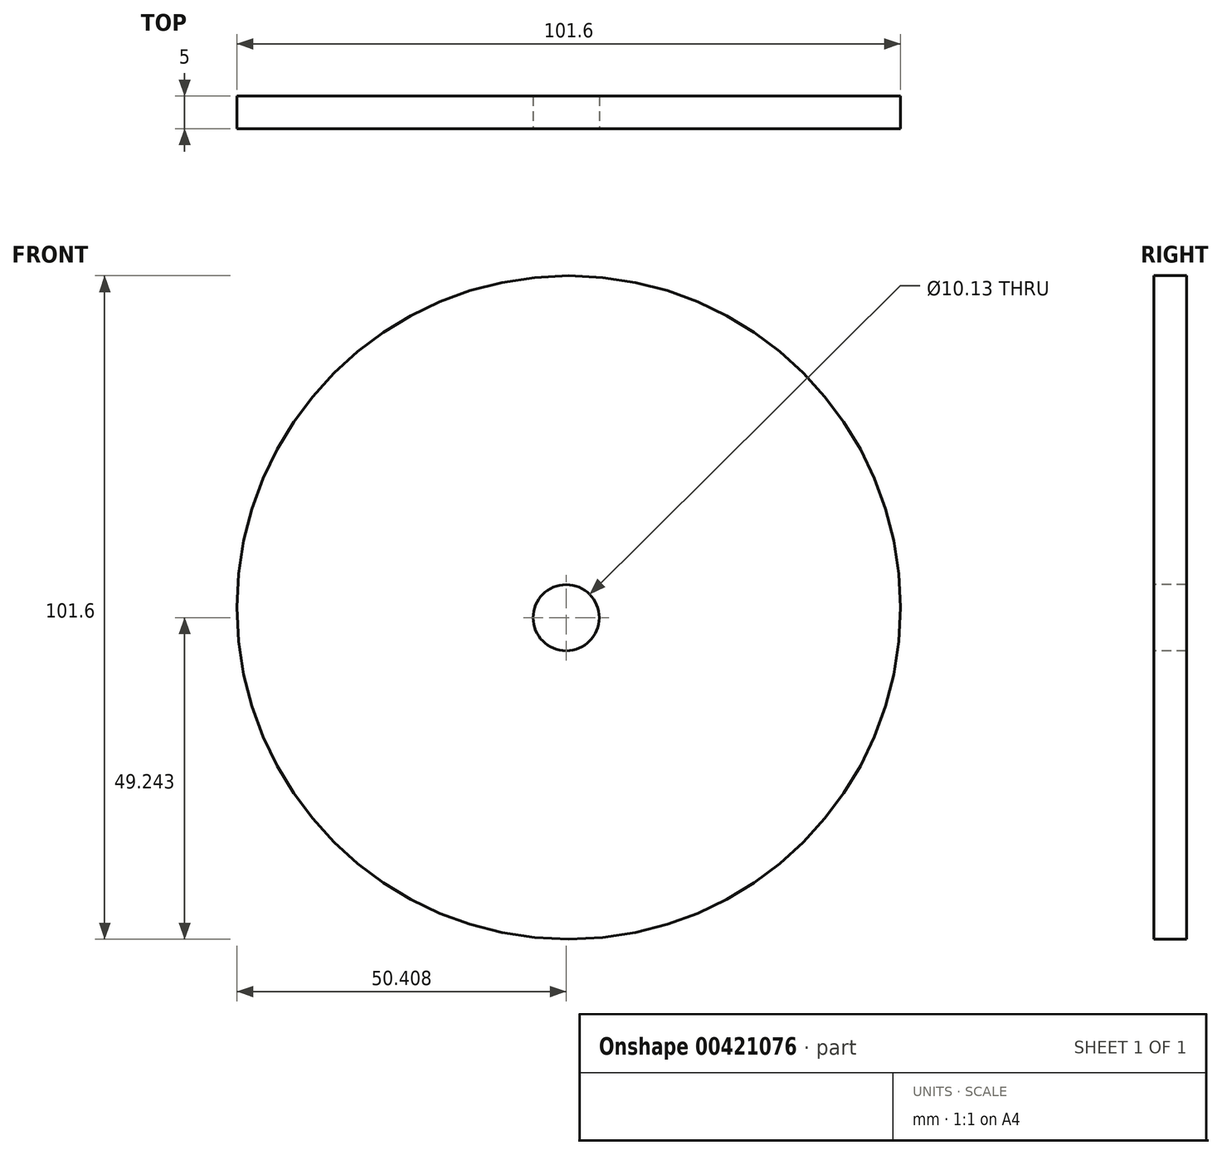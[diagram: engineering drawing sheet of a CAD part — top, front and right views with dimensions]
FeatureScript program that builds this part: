
annotation { "Feature Type Name" : "Feature", "Feature Type Description" : "" }
export const myFeature = defineFeature(function(context is Context, id is Id, definition is map)
    precondition{}
    {
        {
            var Q0;
            Q0=qCreatedBy(makeId("Front.planeOp"),FACE);
            var sketch = newSketch(context, id + "F0", { "sketchPlane" : qUnion([Q0])});
            skCircle(sketch, "E0", {"center": v(-20.32, 98.2) * mm, "radius": 50.8 * mm});
            skSolve(sketch);
        }
        {
            var Q0;
            Q0=makeQuery(id+"F0.imprint","IMPRINT",FACE,{"disambiguationData":[TD([[makeQuery(id+"F0.imprint","IMPRINT",EDGE,{"derivedFrom":sQuery(id+"F0.wireOp",EDGE,"E0")}),1.0]])]});
            extrude(context, id + "F1", {"entities" : qUnion([Q0]), "depth" : 5 * mm});
        }
        {
            var Q0;
            Q0=makeQuery(id+"F1.opExtrude","CAP_FACE",FACE,{"disambiguationData":[OSD([sQuery(id+"F0.wireOp",EDGE,"E0")])],"isStart":false});
            var sketch = newSketch(context, id + "F2", { "sketchPlane" : qUnion([Q0])});
            skCircle(sketch, "E1", {"center": v(-20.32, 98.2) * mm, "radius": 11.29 * mm});
            skSolve(sketch);
        }
        {
            var Q0;
            Q0=makeQuery(id+"F2.imprint","IMPRINT",FACE,{"disambiguationData":[TD([[makeQuery(id+"F2.imprint","IMPRINT",EDGE,{"derivedFrom":sQuery(id+"F2.wireOp",EDGE,"E1")}),1.0]])]});
            var sketch = newSketch(context, id + "F3", { "sketchPlane" : qUnion([Q0])});
            skCircle(sketch, "E2", {"center": v(-20.71, 96.65) * mm, "radius": 5.06 * mm});
            skSolve(sketch);
        }
        {
            var Q0;
            Q0=makeQuery(id+"F3.imprint","IMPRINT",FACE,{"disambiguationData":[TD([[makeQuery(id+"F3.imprint","IMPRINT",EDGE,{"derivedFrom":sQuery(id+"F3.wireOp",EDGE,"E2")}),1.0]])]});
            extrude(context, id + "F4", {"entities" : qUnion([Q0]), "operationType" : NewBodyOperationType.REMOVE, "endBound" : BoundingType.THROUGH_ALL, "oppositeDirection" : true, "depth" : 25.4 * mm});
        }
    });
